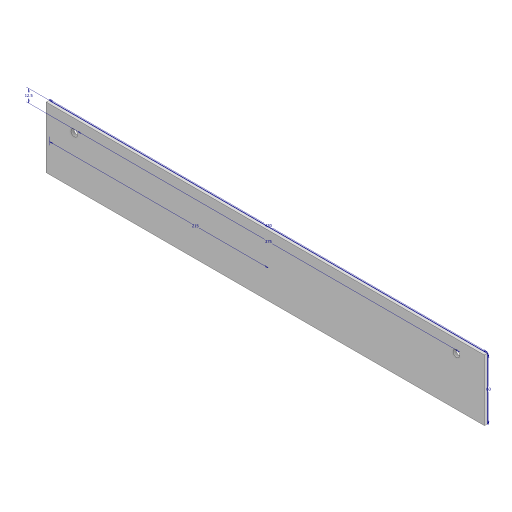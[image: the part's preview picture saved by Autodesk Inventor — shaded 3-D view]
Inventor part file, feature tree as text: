
AUTODESK INVENTOR PART (.ipt)
format: ipt  version: 2023 (Build 270158000, 158)  size: 89,600 bytes
history: native  units: mm
features: sketch x1, extrude x1, hole x1
ambient origin geometry x8: Origin, YZ Plane, XZ Plane, XY Plane, X Axis, Y Axis, Z Axis, Center Point
bodies: Solid1 (feature_tree)
feature tree (3):
  sketch  "Sketch1"  dims[d0=430.0mm d1=60.0mm d2=20.0mm d4=375.0mm d5=10.0mm d7=10.0mm d9=215.0mm d10=12.5mm d11=3.0mm d12=0.0mm d13=6.6mm d14=6.0mm d15=12.6mm d16=2.0mm d17=90.0deg d18=8.0mm d19=0.0mm]
  extrude  "Extrusion1"  Depth=60.0mm
  hole  "Hole1"  [1 undecoded]
note: 1 required parameter value undecoded (feature->parameter linkage not recoverable at this tier; creation-order binding heuristic only, values carry confidence <= 0.55)
